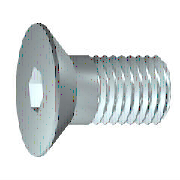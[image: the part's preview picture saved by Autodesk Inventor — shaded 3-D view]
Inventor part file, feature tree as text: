
AUTODESK INVENTOR PART (.ipt)
format: ipt  version: 2022 (Build 260153000, 153)  size: 196,608 bytes
history: native  units: mm (DEFAULTED — no unit token found)
features: other x4, sketch x3, fillet x1, chamfer x1
ambient origin geometry x8: Origin, YZ Plane, XZ Plane, XY Plane, X Axis, Y Axis, Z Axis, Center Point
bodies: Solid1 (feature_tree)
feature tree (9):
  sketch  "Sketch1"  dims[d2=3.0mm]
  other  "WorkPoint1"
  sketch  "Sketch2"  dims[d4=1.5mm]
  fillet  "Fillet1"  [1 undecoded]
  chamfer  "Chamfer1"  Angle=360.0deg  [1 undecoded]
  other  "MSC_A1"
  other  "MSC_PF1"
  other  "MSC_PT1"
  sketch  "Sketch3"  dims[d6=8.0mm d8=360.0deg d9=0.0mm d10=2.0mm d11=2.0mm d12=120.0deg d13=120.0deg d14=120.0deg d15=120.0deg d16=1.2mm d17=0.0mm d18=0.1mm d19=0.25mm d20=45.0deg d35=0.0mm d37=0.0mm d38=0.0mm d39=0.25mm d40=0.0mm d41=0.0mm d42=0.0mm d43=45.0deg d44=3.0mm d45=1.5mm d46=8.0mm d47=0.0mm d48=0.0mm]
note: 2 required parameter values undecoded (feature->parameter linkage not recoverable at this tier; creation-order binding heuristic only, values carry confidence <= 0.55)
